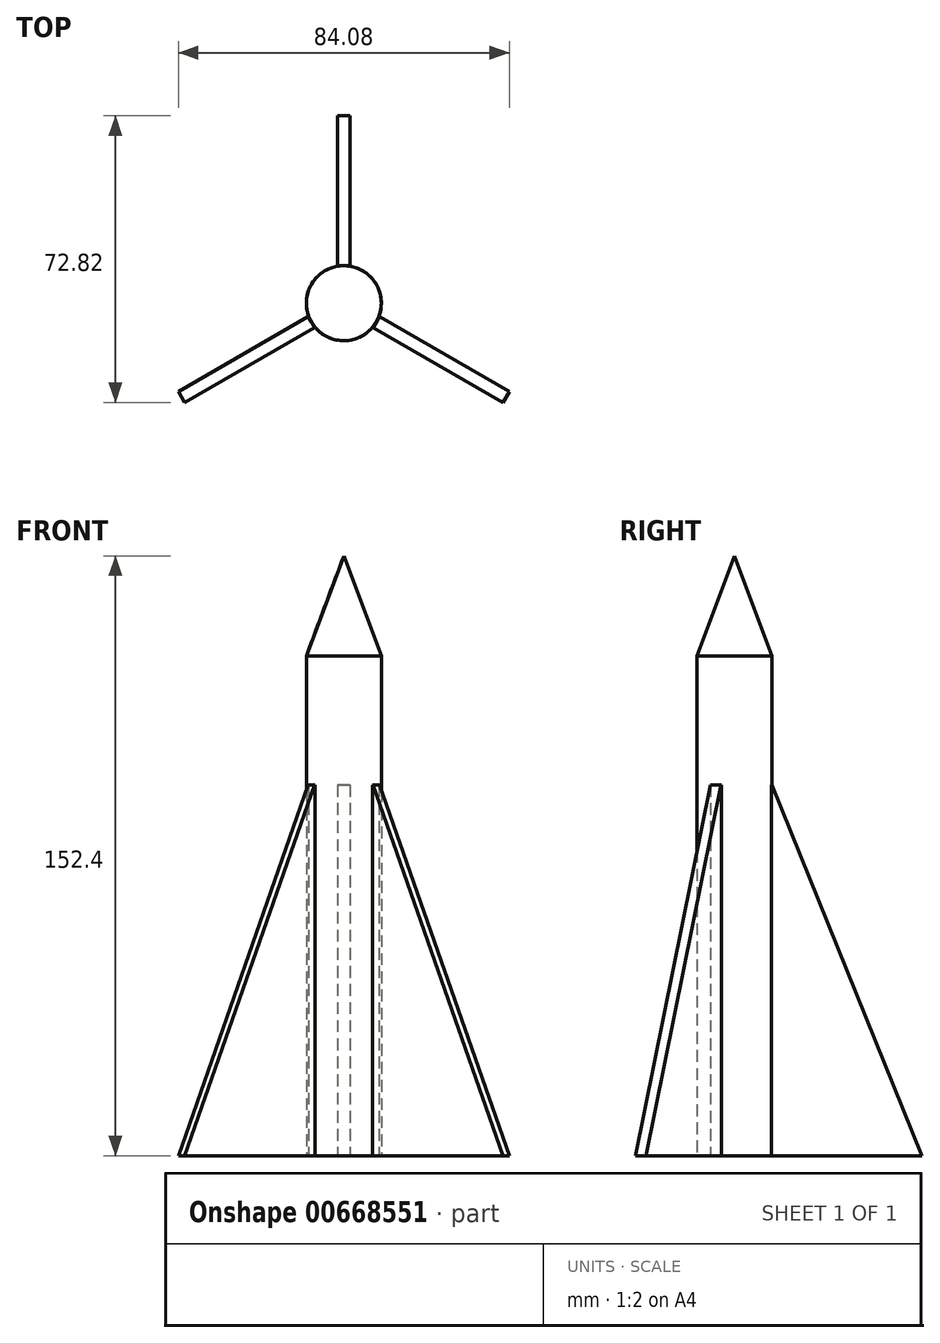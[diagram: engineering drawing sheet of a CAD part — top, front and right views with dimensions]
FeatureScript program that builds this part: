
annotation { "Feature Type Name" : "Feature", "Feature Type Description" : "" }
export const myFeature = defineFeature(function(context is Context, id is Id, definition is map)
    precondition{}
    {
        {
            var Q0;
            Q0=qCreatedBy(makeId("Top.planeOp"),FACE);
            var sketch = newSketch(context, id + "F0", { "sketchPlane" : qUnion([Q0])});
            skCircle(sketch, "E0", {"center": v(0, 0) * mm, "radius": 9.52 * mm});
            skSolve(sketch);
        }
        {
            var Q0;
            Q0=qSketchRegion(id+"F0",true);
            extrude(context, id + "F1", {"entities" : qUnion([Q0]), "depth" : 127 * mm, "offsetDistance" : 25.4 * mm});
        }
        {
            var Q0;
            Q0=qCreatedBy(makeId("Front.planeOp"),FACE);
            var sketch = newSketch(context, id + "F2", { "sketchPlane" : qUnion([Q0])});
            skLineSegment(sketch, "E1.0.0", {"start": v(-9.52, 127) * mm, "end": v(9.52, 127) * mm});
            skLineSegment(sketch, "E2", {"start": v(-9.53, 127) * mm, "end": v(0, 152.4) * mm});
            skLineSegment(sketch, "E3", {"start": v(0, 127) * mm, "end": v(0, 152.4) * mm});
            skSolve(sketch);
        }
        {
            var Q0;
            {var subQ0=sQuery(id+"F2.wireOp",EDGE,"E2");Q0=makeQuery(id+"F2.imprint","IMPRINT",FACE,{"disambiguationData":[TD([[makeQuery(id+"F2.imprint","IMPRINT",EDGE,{"derivedFrom":subQ0}),-1.0]])]});}
            var Q1;
            Q1=sQuery(id+"F2.wireOp",EDGE,"E3");
            revolve(context, id + "F3", {"operationType" : NewBodyOperationType.ADD, "entities" : qUnion([Q0]), "axis" : qUnion([Q1]), "revolveType" : RevolveType.FULL});
        }
        {
            var Q0;
            Q0=qCreatedBy(makeId("Right.planeOp"),FACE);
            var sketch = newSketch(context, id + "F4", { "sketchPlane" : qUnion([Q0])});
            skLineSegment(sketch, "E4", {"start": v(-9.52, 0) * mm, "end": v(-9.52, 127) * mm});
            skLineSegment(sketch, "E5", {"start": v(9.52, 188.37) * mm, "end": v(9.52, 0) * mm});
            skLineSegment(sketch, "E6", {"start": v(9.53, 0) * mm, "end": v(47.62, 0) * mm});
            skLineSegment(sketch, "E7", {"start": v(47.63, 0) * mm, "end": v(9.52, 94.19) * mm});
            skLineSegment(sketch, "E8", {"start": v(9.52, 94.19) * mm, "end": v(3.64, 94.19) * mm});
            skLineSegment(sketch, "E9", {"start": v(3.64, 94.19) * mm, "end": v(3.64, 0) * mm});
            skLineSegment(sketch, "E10", {"start": v(3.64, 0) * mm, "end": v(9.52, 0) * mm});
            skSolve(sketch);
        }
        {
            var Q0;
            Q0=qSketchRegion(id+"F4",true);
            extrude(context, id + "F5", {"entities" : qUnion([Q0]), "operationType" : NewBodyOperationType.ADD, "endBound" : BoundingType.SYMMETRIC, "depth" : 3.17 * mm, "offsetDistance" : 25.4 * mm});
        }
        {
            var Q0;
            Q0=makeQuery(id+"F1.opExtrude","SWEPT_BODY",BODY,{"disambiguationData":[OSD([sQuery(id+"F0.wireOp",EDGE,"E0")])]});
            var Q1;
            Q1=makeQuery(id+"F1.opExtrude","SWEPT_FACE",FACE,{"disambiguationData":[OSD([sQuery(id+"F0.wireOp",EDGE,"E0")])]});
            circularPattern(context, id + "F6", {"entities" : qUnion([Q0]), "axis" : qUnion([Q1]), "angle" : 360 * degree, "instanceCount" : 3, "equalSpace" : true});
        }
    });
